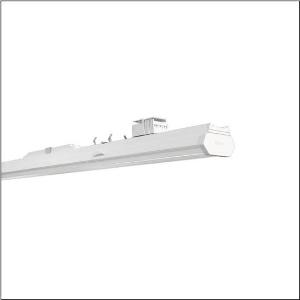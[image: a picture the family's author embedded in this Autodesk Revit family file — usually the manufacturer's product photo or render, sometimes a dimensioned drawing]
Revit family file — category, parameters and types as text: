
# Revit family: licross_r__11_protected_ho_51tp13mn4gxs_4b4b
name_source: partatom
category: Lighting Fixtures
units: mm (PartAtom-declared; Revit-internal decimal feet)

## family parameters
Cut with Voids When Loaded = No
Host = Face
Light Source = No
Part Type = Normal
Room Calculation Point = No
Round Connector Dimension = Use Diameter
Shared = No

## types (1)
- --- (1 x LED, 16110 lm, 87.4 W, 4000K)
    Apparent Load = 87 VA
    CIE Flux Codes = 89 96 99 100 99
    Color Rendering = 80
    Color Temperature = 4000K
    Default Elevation = 1800 mm
    Description = Licross® 11 Protected HO, luminaire insert, of sheet steel, galvanised, coil coated, white, length: 1.500mm, width: 90mm, height: 101mm, LED rated luminous flux: 16.110lm, light colour: 840, control gear: ON/OFF Multilumen, with plug, 3-pole, with phase selection, mains connection: 220..240V, AC, 50/60Hz, rated input power: 87W, halogen-free wiring, primary light control with lens, of plastic, primary optical cover: cover, of PMMA, light emission: direct distribution, primary light characteristic: symmetric, protection rating (complete): IP64, insulation class (complete): insulation class I (protective earthing), certification: CE, ENEC, VDE, UKCA, protection symbol: D if used in an environment with conductive dust loads with corresponding accessories, impact resistance: IK06, permissible ambient temperature for indoor applications: -35..+35°C, corresponds to IFS (International Featured Standards) requirements for safety and quality in the food industry, reducing of maximum allowable ambient temperature of 5°C with ceiling mounting, LABS conformity tested according to VDMA 24364:2018-05, packaging unit: 1 piece
    Height = 92 mm
    Lamp = 1 x LED
    Lamp Light Flux = 16110 lm
    Lamp Power = 87.4 W
    Lamp count = 1
    Length = 1500 mm
    Luminous efficacy = 184 lm/W
    Manufacturer = Siteco
    ModVariant = No
    Model = 51TP13MN4GXS
    Mounting Place = Ceiling
    Mounting Type = Pendant
    Number of Poles = 1
    OnlyDefault = Yes
    Power Factor = 1
    Product Name = Licross® 11 Protected HO
    Product group = luminaire insert
    ProductGroupID = 901
    Protection Class = Protection class I
    Protection Degree = IP 64
    RLX_Detail_Level = 1
    RLX_Emergency_Light_Flux = 0 lm
    RLX_Emergency_Type = 0
    RLX_Emergency_Type_DB = No
    RlxData = <blob elided: 21941 chars, md5=239f1b38>
    Socket = socket
    Standby Power = 0 W
    System Light Flux = 16110 lm
    System Power = 87 W
    Type Comments = factory setting: luminous flux: 100 % | (A | C | E) | 203 mA
    Type Image = l_1256148.jpg
    URL = http://relux.com
    VarID = @adj_019231
    Voltage = 0 V
    Weight = 0.00 kg
    Width = 88 mm

## geometry (parser evidence)
native form markers: Blend x4, Sweep x11
no freeform markers — native parametric forms only
